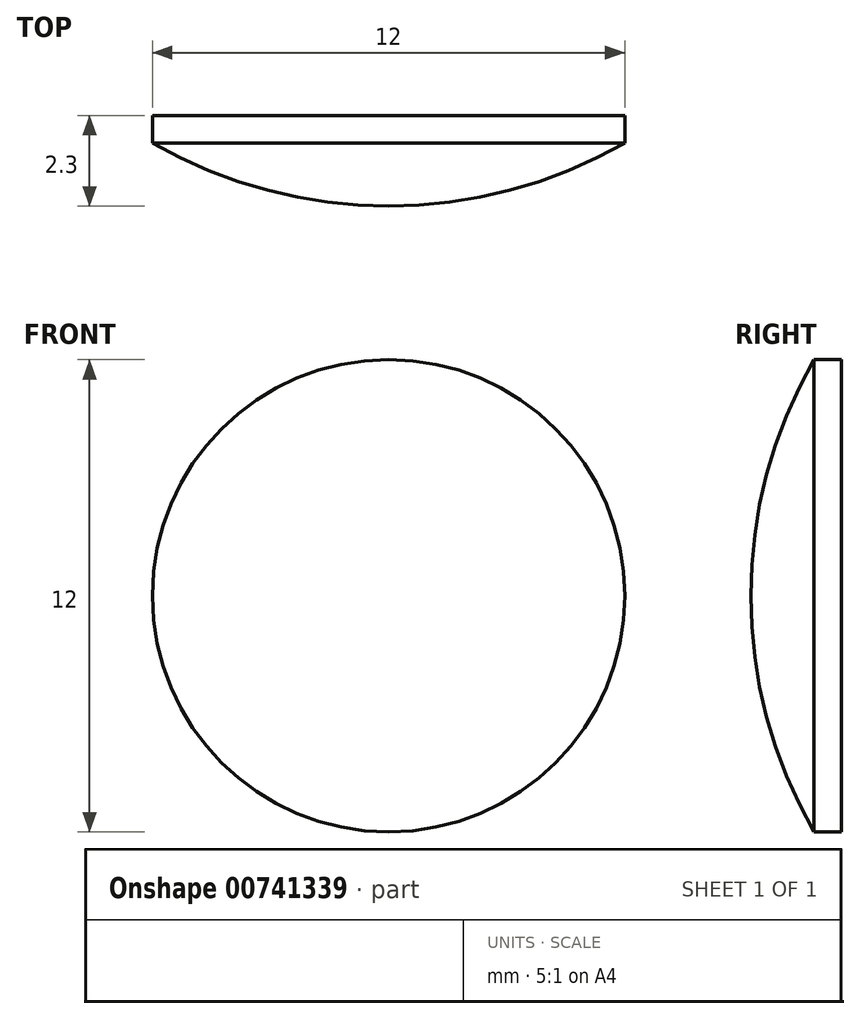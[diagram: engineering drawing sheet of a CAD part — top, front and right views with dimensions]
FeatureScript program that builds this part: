
annotation { "Feature Type Name" : "Feature", "Feature Type Description" : "" }
export const myFeature = defineFeature(function(context is Context, id is Id, definition is map)
    precondition{}
    {
        {
            var Q0;
            Q0=qCreatedBy(makeId("Top.planeOp"),FACE);
            var sketch = newSketch(context, id + "F0", { "sketchPlane" : qUnion([Q0])});
            skCircle(sketch, "E0", {"center": v(0, 0) * mm, "radius": 12 * mm});
            skLineSegment(sketch, "E1", {"start": v(0, 0) * mm, "end": v(-15.57, 0) * mm});
            skLineSegment(sketch, "E2", {"start": v(-15.57, 0) * mm, "end": v(14.8, 0) * mm});
            skSolve(sketch);
        }
        {
            var Q0;
            {var subQ0=sQuery(id+"F0.wireOp",EDGE,"E2");var subQ4=makeQuery(id+"F0.imprint","IMPRINT",VERTEX,{"derivedFrom":subQ0});Q0=makeQuery(id+"F0.imprint","IMPRINT",FACE,{"disambiguationData":[TD([[makeQuery(id+"F0.imprint","IMPRINT",EDGE,{"disambiguationData":[TD([[subQ4,1.0]])],"derivedFrom":subQ0}),-1.0]])]});}
            var Q1;
            Q1=sQuery(id+"F0.wireOp",EDGE,"E2");
            revolve(context, id + "F1", {"surfaceOperationType" : NewSurfaceOperationType.NEW, "entities" : qUnion([Q0]), "axis" : qUnion([Q1]), "revolveType" : RevolveType.FULL});
        }
        {
            var Q0;
            Q0=qCreatedBy(makeId("Front.planeOp"),FACE);
            var sketch = newSketch(context, id + "F2", { "sketchPlane" : qUnion([Q0])});
            skCircle(sketch, "E3", {"center": v(0, 0) * mm, "radius": 12.5 * mm});
            skSolve(sketch);
        }
        {
            var Q0;
            Q0=qSketchRegion(id+"F2",true);
            var Q1;
            Q1=makeQuery(id+"F1.opRevolve","SWEPT_FACE",FACE,{"disambiguationData":[OSD([sQuery(id+"F0.wireOp",EDGE,"E0")])]});
            extrude(context, id + "F3", {"entities" : qUnion([Q0]), "operationType" : NewBodyOperationType.INTERSECT, "endBound" : BoundingType.UP_TO_SURFACE, "depth" : 25 * mm, "endBoundEntityFace" : qUnion([Q1]), "offsetDistance" : 25 * mm});
        }
        {
            var Q0;
            Q0=qCreatedBy(makeId("Front.planeOp"),FACE);
            var sketch = newSketch(context, id + "F4", { "sketchPlane" : qUnion([Q0])});
            skCircle(sketch, "E4", {"center": v(0, 0) * mm, "radius": 25 * mm});
            skSolve(sketch);
        }
        {
            var Q0;
            Q0=qSketchRegion(id+"F4",true);
            extrude(context, id + "F5", {"entities" : qUnion([Q0]), "operationType" : NewBodyOperationType.REMOVE, "depth" : 9.7 * mm, "offsetDistance" : 25 * mm});
        }
        {
            var Q0;
            Q0=qCreatedBy(makeId("Front.planeOp"),FACE);
            var sketch = newSketch(context, id + "F6", { "sketchPlane" : qUnion([Q0])});
            skCircle(sketch, "E5", {"center": v(0, 0) * mm, "radius": 6 * mm});
            skSolve(sketch);
        }
        {
            var Q0;
            Q0 = qSketchRegion(id + "F6", true);
            extrude(context, id + "F7", {"entities" : qUnion([Q0]), "operationType" : NewBodyOperationType.INTERSECT, "depth" : 25 * mm, "offsetDistance" : 25 * mm});
        }
    });
